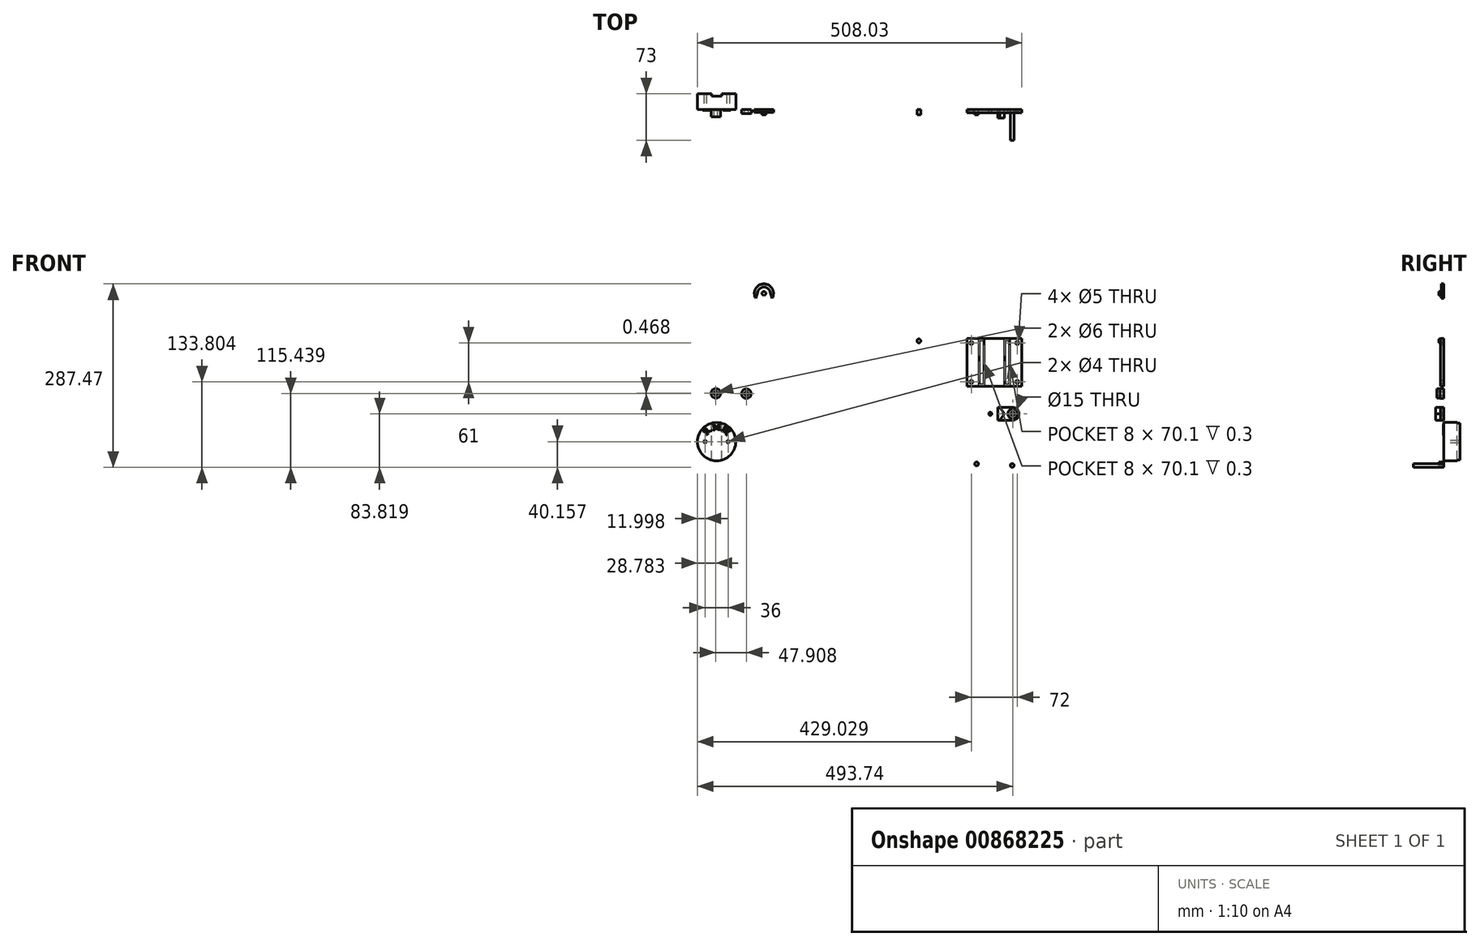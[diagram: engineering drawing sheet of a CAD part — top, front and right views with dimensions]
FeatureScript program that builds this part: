
annotation { "Feature Type Name" : "Feature", "Feature Type Description" : "" }
export const myFeature = defineFeature(function(context is Context, id is Id, definition is map)
    precondition{}
    {
        {
            var Q0;
            Q0=qCreatedBy(makeId("Front.planeOp"),FACE);
            var sketch = newSketch(context, id + "F0", { "sketchPlane" : qUnion([Q0])});
            skCircle(sketch, "E0", {"center": v(126.75, 123.56) * mm, "radius": 3 * mm});
            skLineSegment(sketch, "E1", {"start": v(91.75, 73.56) * mm, "end": v(161.75, 73.56) * mm});
            skLineSegment(sketch, "E2", {"start": v(161.75, 73.56) * mm, "end": v(161.75, 74.2) * mm});
            skLineSegment(sketch, "E3", {"start": v(91.75, 73.56) * mm, "end": v(91.75, 74.2) * mm});
            skLineSegment(sketch, "E4", {"start": v(105.95, 87.96) * mm, "end": v(117.15, 126.36) * mm});
            skLineSegment(sketch, "E5", {"start": v(136.35, 126.36) * mm, "end": v(147.55, 87.96) * mm});
            skArc(sketch, "E6", {"start": v(147.55, 87.96) * mm, "mid": v(152.83, 79.2) * mm, "end": v(161.75, 74.2) * mm});
            skArc(sketch, "E7", {"start": v(91.75, 74.2) * mm, "mid": v(100.67, 79.2) * mm, "end": v(105.95, 87.96) * mm});
            skArc(sketch, "E8", {"start": v(136.35, 126.36) * mm, "mid": v(126.75, 133.56) * mm, "end": v(117.15, 126.36) * mm});
            skSolve(sketch);
        }
        {
            var Q0;
            Q0=makeQuery(id+"F0.imprint","IMPRINT",FACE,{"disambiguationData":[TD([[makeQuery(id+"F0.imprint","IMPRINT",EDGE,{"derivedFrom":sQuery(id+"F0.wireOp",EDGE,"E0")}),1.0]])]});
            extrude(context, id + "F1", {"entities" : qUnion([Q0]), "depth" : 8 * mm, "offsetDistance" : 25 * mm});
        }
        {
            var Q0;
            Q0=qCreatedBy(makeId("Front.planeOp"),FACE);
            var sketch = newSketch(context, id + "F2", { "sketchPlane" : qUnion([Q0])});
            skCircle(sketch, "E9", {"center": v(217.17, -69.3) * mm, "radius": 3 * mm});
            skLineSegment(sketch, "E10", {"start": v(222.17, -46.8) * mm, "end": v(228.17, -69.3) * mm});
            skLineSegment(sketch, "E11", {"start": v(228.17, -69.3) * mm, "end": v(222.17, -91.8) * mm});
            skLineSegment(sketch, "E12", {"start": v(89.17, -61.3) * mm, "end": v(196.17, -61.3) * mm});
            skArc(sketch, "E13", {"start": v(89.17, -61.3) * mm, "mid": v(83.52, -63.64) * mm, "end": v(81.17, -69.3) * mm});
            skLineSegment(sketch, "E14", {"start": v(89.17, -77.3) * mm, "end": v(196.17, -77.3) * mm});
            skArc(sketch, "E15", {"start": v(81.17, -69.3) * mm, "mid": v(83.52, -74.96) * mm, "end": v(89.17, -77.3) * mm});
            skLineSegment(sketch, "E16", {"start": v(214.17, -46.8) * mm, "end": v(222.17, -46.8) * mm});
            skLineSegment(sketch, "E17", {"start": v(214.17, -91.8) * mm, "end": v(222.17, -91.8) * mm});
            skLineSegment(sketch, "E18", {"start": v(222.17, -91.8) * mm, "end": v(214.17, -91.8) * mm});
            skLineSegment(sketch, "E19", {"start": v(196.17, -61.3) * mm, "end": v(214.17, -46.8) * mm});
            skLineSegment(sketch, "E20", {"start": v(214.17, -91.8) * mm, "end": v(196.17, -77.3) * mm});
            skSolve(sketch);
        }
        {
            var Q0;
            Q0=makeQuery(id+"F2.imprint","IMPRINT",FACE,{"disambiguationData":[TD([[makeQuery(id+"F2.imprint","IMPRINT",EDGE,{"derivedFrom":sQuery(id+"F2.wireOp",EDGE,"E9")}),1.0]])]});
            extrude(context, id + "F3", {"entities" : qUnion([Q0]), "depth" : 8 * mm, "offsetDistance" : 25 * mm});
        }
        {
            var Q0;
            Q0=qCreatedBy(makeId("Front.planeOp"),FACE);
            var sketch = newSketch(context, id + "F4", { "sketchPlane" : qUnion([Q0])});
            skCircle(sketch, "E21", {"center": v(272.88, -71.54) * mm, "radius": 3 * mm});
            skSolve(sketch);
        }
        {
            var Q0;
            Q0=makeQuery(id+"F4.imprint","IMPRINT",FACE,{"disambiguationData":[TD([[makeQuery(id+"F4.imprint","IMPRINT",EDGE,{"derivedFrom":sQuery(id+"F4.wireOp",EDGE,"E21")}),1.0]])]});
            extrude(context, id + "F5", {"entities" : qUnion([Q0]), "depth" : 48 * mm, "offsetDistance" : 25 * mm});
        }
        {
            var Q0;
            Q0=qCreatedBy(makeId("Front.planeOp"),FACE);
            var sketch = newSketch(context, id + "F6", { "sketchPlane" : qUnion([Q0])});
            skLineSegment(sketch, "E22", {"start": v(-199.9, -17.86) * mm, "end": v(-201.48, -19.46) * mm});
            skLineSegment(sketch, "E23", {"start": v(-201.48, -19.46) * mm, "end": v(-206.3, -18.72) * mm});
            skLineSegment(sketch, "E24", {"start": v(-206.3, -18.72) * mm, "end": v(-206.66, -19.1) * mm});
            skLineSegment(sketch, "E25", {"start": v(-206.66, -19.1) * mm, "end": v(-206.78, -19.21) * mm});
            skLineSegment(sketch, "E26", {"start": v(-206.78, -19.21) * mm, "end": v(-206.92, -19.34) * mm});
            skLineSegment(sketch, "E27", {"start": v(-206.92, -19.34) * mm, "end": v(-205.18, -21.07) * mm});
            skLineSegment(sketch, "E28", {"start": v(-205.18, -21.07) * mm, "end": v(-204.91, -21.32) * mm});
            skLineSegment(sketch, "E29", {"start": v(-204.91, -21.32) * mm, "end": v(-204.8, -21.42) * mm});
            skLineSegment(sketch, "E30", {"start": v(-204.8, -21.42) * mm, "end": v(-204.69, -21.5) * mm});
            skLineSegment(sketch, "E31", {"start": v(-204.69, -21.5) * mm, "end": v(-204.59, -21.56) * mm});
            skLineSegment(sketch, "E32", {"start": v(-204.59, -21.56) * mm, "end": v(-204.5, -21.6) * mm});
            skLineSegment(sketch, "E33", {"start": v(-204.5, -21.6) * mm, "end": v(-204.42, -21.63) * mm});
            skLineSegment(sketch, "E34", {"start": v(-204.42, -21.63) * mm, "end": v(-204.35, -21.64) * mm});
            skLineSegment(sketch, "E35", {"start": v(-204.35, -21.64) * mm, "end": v(-204.26, -21.65) * mm});
            skLineSegment(sketch, "E36", {"start": v(-204.26, -21.65) * mm, "end": v(-204.17, -21.63) * mm});
            skLineSegment(sketch, "E37", {"start": v(-204.17, -21.63) * mm, "end": v(-204.08, -21.61) * mm});
            skLineSegment(sketch, "E38", {"start": v(-204.08, -21.61) * mm, "end": v(-204, -21.58) * mm});
            skLineSegment(sketch, "E39", {"start": v(-204, -21.58) * mm, "end": v(-203.9, -21.53) * mm});
            skLineSegment(sketch, "E40", {"start": v(-203.9, -21.53) * mm, "end": v(-203.82, -21.48) * mm});
            skLineSegment(sketch, "E41", {"start": v(-203.82, -21.48) * mm, "end": v(-203.74, -21.41) * mm});
            skLineSegment(sketch, "E42", {"start": v(-203.74, -21.41) * mm, "end": v(-203.66, -21.33) * mm});
            skLineSegment(sketch, "E43", {"start": v(-203.66, -21.33) * mm, "end": v(-203.42, -21.1) * mm});
            skLineSegment(sketch, "E44", {"start": v(-203.42, -21.1) * mm, "end": v(-203.26, -21.26) * mm});
            skLineSegment(sketch, "E45", {"start": v(-203.26, -21.26) * mm, "end": v(-205.8, -23.83) * mm});
            skLineSegment(sketch, "E46", {"start": v(-205.8, -23.83) * mm, "end": v(-205.97, -23.67) * mm});
            skLineSegment(sketch, "E47", {"start": v(-205.97, -23.67) * mm, "end": v(-205.75, -23.45) * mm});
            skLineSegment(sketch, "E48", {"start": v(-205.75, -23.45) * mm, "end": v(-205.66, -23.35) * mm});
            skLineSegment(sketch, "E49", {"start": v(-205.66, -23.35) * mm, "end": v(-205.59, -23.25) * mm});
            skLineSegment(sketch, "E50", {"start": v(-205.59, -23.25) * mm, "end": v(-205.53, -23.16) * mm});
            skLineSegment(sketch, "E51", {"start": v(-205.53, -23.16) * mm, "end": v(-205.49, -23.06) * mm});
            skLineSegment(sketch, "E52", {"start": v(-205.49, -23.06) * mm, "end": v(-205.46, -22.96) * mm});
            skLineSegment(sketch, "E53", {"start": v(-205.46, -22.96) * mm, "end": v(-205.44, -22.86) * mm});
            skLineSegment(sketch, "E54", {"start": v(-205.44, -22.86) * mm, "end": v(-205.44, -22.76) * mm});
            skLineSegment(sketch, "E55", {"start": v(-205.44, -22.76) * mm, "end": v(-205.46, -22.66) * mm});
            skLineSegment(sketch, "E56", {"start": v(-205.46, -22.66) * mm, "end": v(-205.47, -22.6) * mm});
            skLineSegment(sketch, "E57", {"start": v(-205.47, -22.6) * mm, "end": v(-205.5, -22.52) * mm});
            skLineSegment(sketch, "E58", {"start": v(-205.5, -22.52) * mm, "end": v(-205.62, -22.36) * mm});
            skLineSegment(sketch, "E59", {"start": v(-205.62, -22.36) * mm, "end": v(-205.79, -22.15) * mm});
            skLineSegment(sketch, "E60", {"start": v(-205.79, -22.15) * mm, "end": v(-206.01, -21.92) * mm});
            skLineSegment(sketch, "E61", {"start": v(-206.01, -21.92) * mm, "end": v(-209.9, -18.08) * mm});
            skLineSegment(sketch, "E62", {"start": v(-209.9, -18.08) * mm, "end": v(-210.16, -17.83) * mm});
            skLineSegment(sketch, "E63", {"start": v(-210.16, -17.83) * mm, "end": v(-210.28, -17.74) * mm});
            skLineSegment(sketch, "E64", {"start": v(-210.28, -17.74) * mm, "end": v(-210.39, -17.65) * mm});
            skLineSegment(sketch, "E65", {"start": v(-210.39, -17.65) * mm, "end": v(-210.49, -17.6) * mm});
            skLineSegment(sketch, "E66", {"start": v(-210.49, -17.6) * mm, "end": v(-210.57, -17.55) * mm});
            skLineSegment(sketch, "E67", {"start": v(-210.57, -17.55) * mm, "end": v(-210.65, -17.52) * mm});
            skLineSegment(sketch, "E68", {"start": v(-210.65, -17.52) * mm, "end": v(-210.72, -17.5) * mm});
            skLineSegment(sketch, "E69", {"start": v(-210.72, -17.5) * mm, "end": v(-210.81, -17.5) * mm});
            skLineSegment(sketch, "E70", {"start": v(-210.81, -17.5) * mm, "end": v(-210.9, -17.52) * mm});
            skLineSegment(sketch, "E71", {"start": v(-210.9, -17.52) * mm, "end": v(-211, -17.54) * mm});
            skLineSegment(sketch, "E72", {"start": v(-211, -17.54) * mm, "end": v(-211.08, -17.58) * mm});
            skLineSegment(sketch, "E73", {"start": v(-211.08, -17.58) * mm, "end": v(-211.17, -17.62) * mm});
            skLineSegment(sketch, "E74", {"start": v(-211.17, -17.62) * mm, "end": v(-211.26, -17.68) * mm});
            skLineSegment(sketch, "E75", {"start": v(-211.26, -17.68) * mm, "end": v(-211.34, -17.75) * mm});
            skLineSegment(sketch, "E76", {"start": v(-211.34, -17.75) * mm, "end": v(-211.43, -17.83) * mm});
            skLineSegment(sketch, "E77", {"start": v(-211.43, -17.83) * mm, "end": v(-211.65, -18.05) * mm});
            skLineSegment(sketch, "E78", {"start": v(-211.65, -18.05) * mm, "end": v(-211.81, -17.9) * mm});
            skLineSegment(sketch, "E79", {"start": v(-211.81, -17.9) * mm, "end": v(-209.65, -15.7) * mm});
            skLineSegment(sketch, "E80", {"start": v(-209.65, -15.7) * mm, "end": v(-209.2, -15.26) * mm});
            skLineSegment(sketch, "E81", {"start": v(-209.2, -15.26) * mm, "end": v(-208.99, -15.07) * mm});
            skLineSegment(sketch, "E82", {"start": v(-208.99, -15.07) * mm, "end": v(-208.8, -14.9) * mm});
            skLineSegment(sketch, "E83", {"start": v(-208.8, -14.9) * mm, "end": v(-208.6, -14.76) * mm});
            skLineSegment(sketch, "E84", {"start": v(-208.6, -14.76) * mm, "end": v(-208.43, -14.63) * mm});
            skLineSegment(sketch, "E85", {"start": v(-208.43, -14.63) * mm, "end": v(-208.27, -14.52) * mm});
            skLineSegment(sketch, "E86", {"start": v(-208.27, -14.52) * mm, "end": v(-208.11, -14.43) * mm});
            skLineSegment(sketch, "E87", {"start": v(-208.11, -14.43) * mm, "end": v(-207.96, -14.36) * mm});
            skLineSegment(sketch, "E88", {"start": v(-207.96, -14.36) * mm, "end": v(-207.81, -14.3) * mm});
            skLineSegment(sketch, "E89", {"start": v(-207.81, -14.3) * mm, "end": v(-207.66, -14.24) * mm});
            skLineSegment(sketch, "E90", {"start": v(-207.66, -14.24) * mm, "end": v(-207.5, -14.2) * mm});
            skLineSegment(sketch, "E91", {"start": v(-207.5, -14.2) * mm, "end": v(-207.34, -14.18) * mm});
            skLineSegment(sketch, "E92", {"start": v(-207.34, -14.18) * mm, "end": v(-207.17, -14.16) * mm});
            skLineSegment(sketch, "E93", {"start": v(-207.17, -14.16) * mm, "end": v(-207, -14.16) * mm});
            skLineSegment(sketch, "E94", {"start": v(-207, -14.16) * mm, "end": v(-206.84, -14.17) * mm});
            skLineSegment(sketch, "E95", {"start": v(-206.84, -14.17) * mm, "end": v(-206.67, -14.19) * mm});
            skLineSegment(sketch, "E96", {"start": v(-206.67, -14.19) * mm, "end": v(-206.5, -14.22) * mm});
            skLineSegment(sketch, "E97", {"start": v(-206.5, -14.22) * mm, "end": v(-206.34, -14.27) * mm});
            skLineSegment(sketch, "E98", {"start": v(-206.34, -14.27) * mm, "end": v(-206.2, -14.33) * mm});
            skLineSegment(sketch, "E99", {"start": v(-206.2, -14.33) * mm, "end": v(-206.04, -14.41) * mm});
            skLineSegment(sketch, "E100", {"start": v(-206.04, -14.41) * mm, "end": v(-205.9, -14.5) * mm});
            skLineSegment(sketch, "E101", {"start": v(-205.9, -14.5) * mm, "end": v(-205.76, -14.61) * mm});
            skLineSegment(sketch, "E102", {"start": v(-205.76, -14.61) * mm, "end": v(-205.63, -14.73) * mm});
            skLineSegment(sketch, "E103", {"start": v(-205.63, -14.73) * mm, "end": v(-205.5, -14.87) * mm});
            skLineSegment(sketch, "E104", {"start": v(-205.5, -14.87) * mm, "end": v(-205.39, -15.02) * mm});
            skLineSegment(sketch, "E105", {"start": v(-205.39, -15.02) * mm, "end": v(-205.29, -15.17) * mm});
            skLineSegment(sketch, "E106", {"start": v(-205.29, -15.17) * mm, "end": v(-205.2, -15.33) * mm});
            skLineSegment(sketch, "E107", {"start": v(-205.2, -15.33) * mm, "end": v(-205.14, -15.5) * mm});
            skLineSegment(sketch, "E108", {"start": v(-205.14, -15.5) * mm, "end": v(-205.08, -15.68) * mm});
            skLineSegment(sketch, "E109", {"start": v(-205.08, -15.68) * mm, "end": v(-205.05, -15.86) * mm});
            skLineSegment(sketch, "E110", {"start": v(-205.05, -15.86) * mm, "end": v(-205.03, -16.04) * mm});
            skLineSegment(sketch, "E111", {"start": v(-205.03, -16.04) * mm, "end": v(-205.02, -16.24) * mm});
            skLineSegment(sketch, "E112", {"start": v(-205.02, -16.24) * mm, "end": v(-205.04, -16.44) * mm});
            skLineSegment(sketch, "E113", {"start": v(-205.04, -16.44) * mm, "end": v(-205.08, -16.64) * mm});
            skLineSegment(sketch, "E114", {"start": v(-205.08, -16.64) * mm, "end": v(-205.13, -16.85) * mm});
            skLineSegment(sketch, "E115", {"start": v(-205.13, -16.85) * mm, "end": v(-205.21, -17.06) * mm});
            skLineSegment(sketch, "E116", {"start": v(-205.21, -17.06) * mm, "end": v(-205.3, -17.28) * mm});
            skLineSegment(sketch, "E117", {"start": v(-205.3, -17.28) * mm, "end": v(-205.42, -17.5) * mm});
            skLineSegment(sketch, "E118", {"start": v(-205.42, -17.5) * mm, "end": v(-205.56, -17.73) * mm});
            skLineSegment(sketch, "E119", {"start": v(-205.56, -17.73) * mm, "end": v(-202.6, -18.2) * mm});
            skLineSegment(sketch, "E120", {"start": v(-202.6, -18.2) * mm, "end": v(-202.13, -18.26) * mm});
            skLineSegment(sketch, "E121", {"start": v(-202.13, -18.26) * mm, "end": v(-201.72, -18.3) * mm});
            skLineSegment(sketch, "E122", {"start": v(-201.72, -18.3) * mm, "end": v(-201.54, -18.3) * mm});
            skLineSegment(sketch, "E123", {"start": v(-201.54, -18.3) * mm, "end": v(-201.38, -18.29) * mm});
            skLineSegment(sketch, "E124", {"start": v(-201.38, -18.29) * mm, "end": v(-201.23, -18.27) * mm});
            skLineSegment(sketch, "E125", {"start": v(-201.23, -18.27) * mm, "end": v(-201.1, -18.25) * mm});
            skLineSegment(sketch, "E126", {"start": v(-201.1, -18.25) * mm, "end": v(-200.97, -18.21) * mm});
            skLineSegment(sketch, "E127", {"start": v(-200.97, -18.21) * mm, "end": v(-200.84, -18.17) * mm});
            skLineSegment(sketch, "E128", {"start": v(-200.84, -18.17) * mm, "end": v(-200.72, -18.12) * mm});
            skLineSegment(sketch, "E129", {"start": v(-200.72, -18.12) * mm, "end": v(-200.59, -18.05) * mm});
            skLineSegment(sketch, "E130", {"start": v(-200.59, -18.05) * mm, "end": v(-200.46, -17.98) * mm});
            skLineSegment(sketch, "E131", {"start": v(-200.46, -17.98) * mm, "end": v(-200.32, -17.9) * mm});
            skLineSegment(sketch, "E132", {"start": v(-200.32, -17.9) * mm, "end": v(-200.06, -17.7) * mm});
            skLineSegment(sketch, "E133", {"start": v(-200.06, -17.7) * mm, "end": v(-199.9, -17.86) * mm});
            skLineSegment(sketch, "E134", {"start": v(-207.2, -19.07) * mm, "end": v(-207.06, -18.92) * mm});
            skLineSegment(sketch, "E135", {"start": v(-207.06, -18.92) * mm, "end": v(-206.95, -18.83) * mm});
            skLineSegment(sketch, "E136", {"start": v(-206.95, -18.83) * mm, "end": v(-206.75, -18.61) * mm});
            skLineSegment(sketch, "E137", {"start": v(-206.75, -18.61) * mm, "end": v(-206.58, -18.4) * mm});
            skLineSegment(sketch, "E138", {"start": v(-206.58, -18.4) * mm, "end": v(-206.43, -18.19) * mm});
            skLineSegment(sketch, "E139", {"start": v(-206.43, -18.19) * mm, "end": v(-206.3, -17.98) * mm});
            skLineSegment(sketch, "E140", {"start": v(-206.3, -17.98) * mm, "end": v(-206.2, -17.77) * mm});
            skLineSegment(sketch, "E141", {"start": v(-206.2, -17.77) * mm, "end": v(-206.12, -17.57) * mm});
            skLineSegment(sketch, "E142", {"start": v(-206.12, -17.57) * mm, "end": v(-206.07, -17.36) * mm});
            skLineSegment(sketch, "E143", {"start": v(-206.07, -17.36) * mm, "end": v(-206.04, -17.16) * mm});
            skLineSegment(sketch, "E144", {"start": v(-206.04, -17.16) * mm, "end": v(-206.04, -16.96) * mm});
            skLineSegment(sketch, "E145", {"start": v(-206.04, -16.96) * mm, "end": v(-206.05, -16.77) * mm});
            skLineSegment(sketch, "E146", {"start": v(-206.05, -16.77) * mm, "end": v(-206.09, -16.6) * mm});
            skLineSegment(sketch, "E147", {"start": v(-206.09, -16.6) * mm, "end": v(-206.14, -16.42) * mm});
            skLineSegment(sketch, "E148", {"start": v(-206.14, -16.42) * mm, "end": v(-206.22, -16.25) * mm});
            skLineSegment(sketch, "E149", {"start": v(-206.22, -16.25) * mm, "end": v(-206.31, -16.09) * mm});
            skLineSegment(sketch, "E150", {"start": v(-206.31, -16.09) * mm, "end": v(-206.43, -15.93) * mm});
            skLineSegment(sketch, "E151", {"start": v(-206.43, -15.93) * mm, "end": v(-206.56, -15.79) * mm});
            skLineSegment(sketch, "E152", {"start": v(-206.56, -15.79) * mm, "end": v(-206.7, -15.66) * mm});
            skLineSegment(sketch, "E153", {"start": v(-206.7, -15.66) * mm, "end": v(-206.85, -15.54) * mm});
            skLineSegment(sketch, "E154", {"start": v(-206.85, -15.54) * mm, "end": v(-207, -15.45) * mm});
            skLineSegment(sketch, "E155", {"start": v(-207, -15.45) * mm, "end": v(-207.16, -15.37) * mm});
            skLineSegment(sketch, "E156", {"start": v(-207.16, -15.37) * mm, "end": v(-207.32, -15.3) * mm});
            skLineSegment(sketch, "E157", {"start": v(-207.32, -15.3) * mm, "end": v(-207.48, -15.27) * mm});
            skLineSegment(sketch, "E158", {"start": v(-207.48, -15.27) * mm, "end": v(-207.65, -15.24) * mm});
            skLineSegment(sketch, "E159", {"start": v(-207.65, -15.24) * mm, "end": v(-207.82, -15.23) * mm});
            skLineSegment(sketch, "E160", {"start": v(-207.82, -15.23) * mm, "end": v(-208, -15.24) * mm});
            skLineSegment(sketch, "E161", {"start": v(-208, -15.24) * mm, "end": v(-208.17, -15.27) * mm});
            skLineSegment(sketch, "E162", {"start": v(-208.17, -15.27) * mm, "end": v(-208.33, -15.32) * mm});
            skLineSegment(sketch, "E163", {"start": v(-208.33, -15.32) * mm, "end": v(-208.5, -15.38) * mm});
            skLineSegment(sketch, "E164", {"start": v(-208.5, -15.38) * mm, "end": v(-208.65, -15.46) * mm});
            skLineSegment(sketch, "E165", {"start": v(-208.65, -15.46) * mm, "end": v(-208.8, -15.56) * mm});
            skLineSegment(sketch, "E166", {"start": v(-208.8, -15.56) * mm, "end": v(-208.95, -15.68) * mm});
            skLineSegment(sketch, "E167", {"start": v(-208.95, -15.68) * mm, "end": v(-209.1, -15.82) * mm});
            skLineSegment(sketch, "E168", {"start": v(-209.1, -15.82) * mm, "end": v(-209.23, -15.96) * mm});
            skLineSegment(sketch, "E169", {"start": v(-209.23, -15.96) * mm, "end": v(-209.38, -16.14) * mm});
            skLineSegment(sketch, "E170", {"start": v(-209.38, -16.14) * mm, "end": v(-209.53, -16.35) * mm});
            skLineSegment(sketch, "E171", {"start": v(-209.53, -16.35) * mm, "end": v(-209.7, -16.6) * mm});
            skLineSegment(sketch, "E172", {"start": v(-209.7, -16.6) * mm, "end": v(-207.2, -19.07) * mm});
            skLineSegment(sketch, "E173", {"start": v(-198.08, -16.28) * mm, "end": v(-197.95, -16.23) * mm});
            skLineSegment(sketch, "E174", {"start": v(-197.95, -16.23) * mm, "end": v(-197.81, -16.21) * mm});
            skLineSegment(sketch, "E175", {"start": v(-197.81, -16.21) * mm, "end": v(-197.68, -16.22) * mm});
            skLineSegment(sketch, "E176", {"start": v(-197.68, -16.22) * mm, "end": v(-197.55, -16.26) * mm});
            skLineSegment(sketch, "E177", {"start": v(-197.55, -16.26) * mm, "end": v(-197.42, -16.32) * mm});
            skLineSegment(sketch, "E178", {"start": v(-197.42, -16.32) * mm, "end": v(-197.32, -16.4) * mm});
            skLineSegment(sketch, "E179", {"start": v(-197.32, -16.4) * mm, "end": v(-197.23, -16.5) * mm});
            skLineSegment(sketch, "E180", {"start": v(-197.23, -16.5) * mm, "end": v(-197.16, -16.61) * mm});
            skLineSegment(sketch, "E181", {"start": v(-197.16, -16.61) * mm, "end": v(-197.1, -16.74) * mm});
            skLineSegment(sketch, "E182", {"start": v(-197.1, -16.74) * mm, "end": v(-197.09, -16.88) * mm});
            skLineSegment(sketch, "E183", {"start": v(-197.09, -16.88) * mm, "end": v(-197.1, -17) * mm});
            skLineSegment(sketch, "E184", {"start": v(-197.1, -17) * mm, "end": v(-197.13, -17.14) * mm});
            skLineSegment(sketch, "E185", {"start": v(-197.13, -17.14) * mm, "end": v(-197.2, -17.27) * mm});
            skLineSegment(sketch, "E186", {"start": v(-197.2, -17.27) * mm, "end": v(-197.27, -17.38) * mm});
            skLineSegment(sketch, "E187", {"start": v(-197.27, -17.38) * mm, "end": v(-197.37, -17.46) * mm});
            skLineSegment(sketch, "E188", {"start": v(-197.37, -17.46) * mm, "end": v(-197.49, -17.53) * mm});
            skLineSegment(sketch, "E189", {"start": v(-197.49, -17.53) * mm, "end": v(-197.62, -17.58) * mm});
            skLineSegment(sketch, "E190", {"start": v(-197.62, -17.58) * mm, "end": v(-197.75, -17.6) * mm});
            skLineSegment(sketch, "E191", {"start": v(-197.75, -17.6) * mm, "end": v(-197.88, -17.6) * mm});
            skLineSegment(sketch, "E192", {"start": v(-197.88, -17.6) * mm, "end": v(-198.02, -17.56) * mm});
            skLineSegment(sketch, "E193", {"start": v(-198.02, -17.56) * mm, "end": v(-198.14, -17.5) * mm});
            skLineSegment(sketch, "E194", {"start": v(-198.14, -17.5) * mm, "end": v(-198.25, -17.42) * mm});
            skLineSegment(sketch, "E195", {"start": v(-198.25, -17.42) * mm, "end": v(-198.34, -17.32) * mm});
            skLineSegment(sketch, "E196", {"start": v(-198.34, -17.32) * mm, "end": v(-198.4, -17.2) * mm});
            skLineSegment(sketch, "E197", {"start": v(-198.4, -17.2) * mm, "end": v(-198.46, -17.07) * mm});
            skLineSegment(sketch, "E198", {"start": v(-198.46, -17.07) * mm, "end": v(-198.48, -16.94) * mm});
            skLineSegment(sketch, "E199", {"start": v(-198.48, -16.94) * mm, "end": v(-198.47, -16.8) * mm});
            skLineSegment(sketch, "E200", {"start": v(-198.47, -16.8) * mm, "end": v(-198.44, -16.67) * mm});
            skLineSegment(sketch, "E201", {"start": v(-198.44, -16.67) * mm, "end": v(-198.38, -16.55) * mm});
            skLineSegment(sketch, "E202", {"start": v(-198.38, -16.55) * mm, "end": v(-198.3, -16.44) * mm});
            skLineSegment(sketch, "E203", {"start": v(-198.3, -16.44) * mm, "end": v(-198.2, -16.35) * mm});
            skLineSegment(sketch, "E204", {"start": v(-198.2, -16.35) * mm, "end": v(-198.08, -16.28) * mm});
            skLineSegment(sketch, "E205", {"start": v(-190.55, -15.85) * mm, "end": v(-193.93, -8.79) * mm});
            skLineSegment(sketch, "E206", {"start": v(-193.93, -8.79) * mm, "end": v(-193.84, -14.43) * mm});
            skLineSegment(sketch, "E207", {"start": v(-193.84, -14.43) * mm, "end": v(-193.83, -14.79) * mm});
            skLineSegment(sketch, "E208", {"start": v(-193.83, -14.79) * mm, "end": v(-193.8, -15.07) * mm});
            skLineSegment(sketch, "E209", {"start": v(-193.8, -15.07) * mm, "end": v(-193.76, -15.18) * mm});
            skLineSegment(sketch, "E210", {"start": v(-193.76, -15.18) * mm, "end": v(-193.73, -15.27) * mm});
            skLineSegment(sketch, "E211", {"start": v(-193.73, -15.27) * mm, "end": v(-193.7, -15.35) * mm});
            skLineSegment(sketch, "E212", {"start": v(-193.7, -15.35) * mm, "end": v(-193.66, -15.4) * mm});
            skLineSegment(sketch, "E213", {"start": v(-193.66, -15.4) * mm, "end": v(-193.6, -15.46) * mm});
            skLineSegment(sketch, "E214", {"start": v(-193.6, -15.46) * mm, "end": v(-193.52, -15.52) * mm});
            skLineSegment(sketch, "E215", {"start": v(-193.52, -15.52) * mm, "end": v(-193.45, -15.56) * mm});
            skLineSegment(sketch, "E216", {"start": v(-193.45, -15.56) * mm, "end": v(-193.36, -15.6) * mm});
            skLineSegment(sketch, "E217", {"start": v(-193.36, -15.6) * mm, "end": v(-193.26, -15.62) * mm});
            skLineSegment(sketch, "E218", {"start": v(-193.26, -15.62) * mm, "end": v(-193.16, -15.64) * mm});
            skLineSegment(sketch, "E219", {"start": v(-193.16, -15.64) * mm, "end": v(-193.05, -15.65) * mm});
            skLineSegment(sketch, "E220", {"start": v(-193.05, -15.65) * mm, "end": v(-192.93, -15.65) * mm});
            skLineSegment(sketch, "E221", {"start": v(-192.93, -15.65) * mm, "end": v(-192.63, -15.65) * mm});
            skLineSegment(sketch, "E222", {"start": v(-192.63, -15.65) * mm, "end": v(-192.62, -15.88) * mm});
            skLineSegment(sketch, "E223", {"start": v(-192.62, -15.88) * mm, "end": v(-195.56, -15.93) * mm});
            skLineSegment(sketch, "E224", {"start": v(-195.56, -15.93) * mm, "end": v(-195.57, -15.7) * mm});
            skLineSegment(sketch, "E225", {"start": v(-195.57, -15.7) * mm, "end": v(-195.27, -15.7) * mm});
            skLineSegment(sketch, "E226", {"start": v(-195.27, -15.7) * mm, "end": v(-195.14, -15.68) * mm});
            skLineSegment(sketch, "E227", {"start": v(-195.14, -15.68) * mm, "end": v(-195.02, -15.67) * mm});
            skLineSegment(sketch, "E228", {"start": v(-195.02, -15.67) * mm, "end": v(-194.91, -15.64) * mm});
            skLineSegment(sketch, "E229", {"start": v(-194.91, -15.64) * mm, "end": v(-194.81, -15.6) * mm});
            skLineSegment(sketch, "E230", {"start": v(-194.81, -15.6) * mm, "end": v(-194.72, -15.56) * mm});
            skLineSegment(sketch, "E231", {"start": v(-194.72, -15.56) * mm, "end": v(-194.64, -15.5) * mm});
            skLineSegment(sketch, "E232", {"start": v(-194.64, -15.5) * mm, "end": v(-194.57, -15.43) * mm});
            skLineSegment(sketch, "E233", {"start": v(-194.57, -15.43) * mm, "end": v(-194.51, -15.35) * mm});
            skLineSegment(sketch, "E234", {"start": v(-194.51, -15.35) * mm, "end": v(-194.48, -15.3) * mm});
            skLineSegment(sketch, "E235", {"start": v(-194.48, -15.3) * mm, "end": v(-194.46, -15.22) * mm});
            skLineSegment(sketch, "E236", {"start": v(-194.46, -15.22) * mm, "end": v(-194.43, -15.13) * mm});
            skLineSegment(sketch, "E237", {"start": v(-194.43, -15.13) * mm, "end": v(-194.42, -15.03) * mm});
            skLineSegment(sketch, "E238", {"start": v(-194.42, -15.03) * mm, "end": v(-194.4, -14.77) * mm});
            skLineSegment(sketch, "E239", {"start": v(-194.4, -14.77) * mm, "end": v(-194.4, -14.44) * mm});
            skLineSegment(sketch, "E240", {"start": v(-194.4, -14.44) * mm, "end": v(-194.48, -8.92) * mm});
            skLineSegment(sketch, "E241", {"start": v(-194.48, -8.92) * mm, "end": v(-194.49, -8.66) * mm});
            skLineSegment(sketch, "E242", {"start": v(-194.49, -8.66) * mm, "end": v(-194.51, -8.44) * mm});
            skLineSegment(sketch, "E243", {"start": v(-194.51, -8.44) * mm, "end": v(-194.56, -8.26) * mm});
            skLineSegment(sketch, "E244", {"start": v(-194.56, -8.26) * mm, "end": v(-194.61, -8.11) * mm});
            skLineSegment(sketch, "E245", {"start": v(-194.61, -8.11) * mm, "end": v(-194.67, -8.03) * mm});
            skLineSegment(sketch, "E246", {"start": v(-194.67, -8.03) * mm, "end": v(-194.74, -7.95) * mm});
            skLineSegment(sketch, "E247", {"start": v(-194.74, -7.95) * mm, "end": v(-194.83, -7.88) * mm});
            skLineSegment(sketch, "E248", {"start": v(-194.83, -7.88) * mm, "end": v(-194.94, -7.82) * mm});
            skLineSegment(sketch, "E249", {"start": v(-194.94, -7.82) * mm, "end": v(-195.07, -7.76) * mm});
            skLineSegment(sketch, "E250", {"start": v(-195.07, -7.76) * mm, "end": v(-195.24, -7.73) * mm});
            skLineSegment(sketch, "E251", {"start": v(-195.24, -7.73) * mm, "end": v(-195.45, -7.71) * mm});
            skLineSegment(sketch, "E252", {"start": v(-195.45, -7.71) * mm, "end": v(-195.7, -7.7) * mm});
            skLineSegment(sketch, "E253", {"start": v(-195.7, -7.7) * mm, "end": v(-195.7, -7.48) * mm});
            skLineSegment(sketch, "E254", {"start": v(-195.7, -7.48) * mm, "end": v(-193.3, -7.44) * mm});
            skLineSegment(sketch, "E255", {"start": v(-193.3, -7.44) * mm, "end": v(-190.13, -14) * mm});
            skLineSegment(sketch, "E256", {"start": v(-190.13, -14) * mm, "end": v(-187.22, -7.35) * mm});
            skLineSegment(sketch, "E257", {"start": v(-187.22, -7.35) * mm, "end": v(-184.83, -7.3) * mm});
            skLineSegment(sketch, "E258", {"start": v(-184.83, -7.3) * mm, "end": v(-184.82, -7.54) * mm});
            skLineSegment(sketch, "E259", {"start": v(-184.82, -7.54) * mm, "end": v(-185.12, -7.54) * mm});
            skLineSegment(sketch, "E260", {"start": v(-185.12, -7.54) * mm, "end": v(-185.25, -7.55) * mm});
            skLineSegment(sketch, "E261", {"start": v(-185.25, -7.55) * mm, "end": v(-185.37, -7.57) * mm});
            skLineSegment(sketch, "E262", {"start": v(-185.37, -7.57) * mm, "end": v(-185.48, -7.6) * mm});
            skLineSegment(sketch, "E263", {"start": v(-185.48, -7.6) * mm, "end": v(-185.58, -7.63) * mm});
            skLineSegment(sketch, "E264", {"start": v(-185.58, -7.63) * mm, "end": v(-185.67, -7.68) * mm});
            skLineSegment(sketch, "E265", {"start": v(-185.67, -7.68) * mm, "end": v(-185.75, -7.74) * mm});
            skLineSegment(sketch, "E266", {"start": v(-185.75, -7.74) * mm, "end": v(-185.82, -7.8) * mm});
            skLineSegment(sketch, "E267", {"start": v(-185.82, -7.8) * mm, "end": v(-185.88, -7.88) * mm});
            skLineSegment(sketch, "E268", {"start": v(-185.88, -7.88) * mm, "end": v(-185.9, -7.94) * mm});
            skLineSegment(sketch, "E269", {"start": v(-185.9, -7.94) * mm, "end": v(-185.94, -8.01) * mm});
            skLineSegment(sketch, "E270", {"start": v(-185.94, -8.01) * mm, "end": v(-185.96, -8.1) * mm});
            skLineSegment(sketch, "E271", {"start": v(-185.96, -8.1) * mm, "end": v(-185.98, -8.2) * mm});
            skLineSegment(sketch, "E272", {"start": v(-185.98, -8.2) * mm, "end": v(-186, -8.47) * mm});
            skLineSegment(sketch, "E273", {"start": v(-186, -8.47) * mm, "end": v(-186, -8.8) * mm});
            skLineSegment(sketch, "E274", {"start": v(-186, -8.8) * mm, "end": v(-185.92, -14.31) * mm});
            skLineSegment(sketch, "E275", {"start": v(-185.92, -14.31) * mm, "end": v(-185.9, -14.66) * mm});
            skLineSegment(sketch, "E276", {"start": v(-185.9, -14.66) * mm, "end": v(-185.88, -14.81) * mm});
            skLineSegment(sketch, "E277", {"start": v(-185.88, -14.81) * mm, "end": v(-185.86, -14.94) * mm});
            skLineSegment(sketch, "E278", {"start": v(-185.86, -14.94) * mm, "end": v(-185.84, -15.06) * mm});
            skLineSegment(sketch, "E279", {"start": v(-185.84, -15.06) * mm, "end": v(-185.8, -15.15) * mm});
            skLineSegment(sketch, "E280", {"start": v(-185.8, -15.15) * mm, "end": v(-185.77, -15.22) * mm});
            skLineSegment(sketch, "E281", {"start": v(-185.77, -15.22) * mm, "end": v(-185.73, -15.28) * mm});
            skLineSegment(sketch, "E282", {"start": v(-185.73, -15.28) * mm, "end": v(-185.66, -15.34) * mm});
            skLineSegment(sketch, "E283", {"start": v(-185.66, -15.34) * mm, "end": v(-185.6, -15.4) * mm});
            skLineSegment(sketch, "E284", {"start": v(-185.6, -15.4) * mm, "end": v(-185.51, -15.44) * mm});
            skLineSegment(sketch, "E285", {"start": v(-185.51, -15.44) * mm, "end": v(-185.43, -15.47) * mm});
            skLineSegment(sketch, "E286", {"start": v(-185.43, -15.47) * mm, "end": v(-185.33, -15.5) * mm});
            skLineSegment(sketch, "E287", {"start": v(-185.33, -15.5) * mm, "end": v(-185.23, -15.52) * mm});
            skLineSegment(sketch, "E288", {"start": v(-185.23, -15.52) * mm, "end": v(-185.11, -15.53) * mm});
            skLineSegment(sketch, "E289", {"start": v(-185.11, -15.53) * mm, "end": v(-185, -15.53) * mm});
            skLineSegment(sketch, "E290", {"start": v(-185, -15.53) * mm, "end": v(-184.7, -15.53) * mm});
            skLineSegment(sketch, "E291", {"start": v(-184.7, -15.53) * mm, "end": v(-184.7, -15.76) * mm});
            skLineSegment(sketch, "E292", {"start": v(-184.7, -15.76) * mm, "end": v(-188.29, -15.81) * mm});
            skLineSegment(sketch, "E293", {"start": v(-188.29, -15.81) * mm, "end": v(-188.29, -15.58) * mm});
            skLineSegment(sketch, "E294", {"start": v(-188.29, -15.58) * mm, "end": v(-188, -15.58) * mm});
            skLineSegment(sketch, "E295", {"start": v(-188, -15.58) * mm, "end": v(-187.86, -15.57) * mm});
            skLineSegment(sketch, "E296", {"start": v(-187.86, -15.57) * mm, "end": v(-187.74, -15.55) * mm});
            skLineSegment(sketch, "E297", {"start": v(-187.74, -15.55) * mm, "end": v(-187.63, -15.53) * mm});
            skLineSegment(sketch, "E298", {"start": v(-187.63, -15.53) * mm, "end": v(-187.53, -15.5) * mm});
            skLineSegment(sketch, "E299", {"start": v(-187.53, -15.5) * mm, "end": v(-187.44, -15.44) * mm});
            skLineSegment(sketch, "E300", {"start": v(-187.44, -15.44) * mm, "end": v(-187.36, -15.39) * mm});
            skLineSegment(sketch, "E301", {"start": v(-187.36, -15.39) * mm, "end": v(-187.3, -15.32) * mm});
            skLineSegment(sketch, "E302", {"start": v(-187.3, -15.32) * mm, "end": v(-187.23, -15.24) * mm});
            skLineSegment(sketch, "E303", {"start": v(-187.23, -15.24) * mm, "end": v(-187.2, -15.18) * mm});
            skLineSegment(sketch, "E304", {"start": v(-187.2, -15.18) * mm, "end": v(-187.18, -15.1) * mm});
            skLineSegment(sketch, "E305", {"start": v(-187.18, -15.1) * mm, "end": v(-187.15, -15.02) * mm});
            skLineSegment(sketch, "E306", {"start": v(-187.15, -15.02) * mm, "end": v(-187.14, -14.91) * mm});
            skLineSegment(sketch, "E307", {"start": v(-187.14, -14.91) * mm, "end": v(-187.12, -14.65) * mm});
            skLineSegment(sketch, "E308", {"start": v(-187.12, -14.65) * mm, "end": v(-187.11, -14.33) * mm});
            skLineSegment(sketch, "E309", {"start": v(-187.11, -14.33) * mm, "end": v(-187.2, -8.68) * mm});
            skLineSegment(sketch, "E310", {"start": v(-187.2, -8.68) * mm, "end": v(-190.35, -15.85) * mm});
            skLineSegment(sketch, "E311", {"start": v(-190.35, -15.85) * mm, "end": v(-190.55, -15.85) * mm});
            skLineSegment(sketch, "E312", {"start": v(-182.17, -16.31) * mm, "end": v(-182.05, -16.38) * mm});
            skLineSegment(sketch, "E313", {"start": v(-182.05, -16.38) * mm, "end": v(-181.95, -16.47) * mm});
            skLineSegment(sketch, "E314", {"start": v(-181.95, -16.47) * mm, "end": v(-181.87, -16.58) * mm});
            skLineSegment(sketch, "E315", {"start": v(-181.87, -16.58) * mm, "end": v(-181.82, -16.7) * mm});
            skLineSegment(sketch, "E316", {"start": v(-181.82, -16.7) * mm, "end": v(-181.78, -16.84) * mm});
            skLineSegment(sketch, "E317", {"start": v(-181.78, -16.84) * mm, "end": v(-181.78, -16.97) * mm});
            skLineSegment(sketch, "E318", {"start": v(-181.78, -16.97) * mm, "end": v(-181.8, -17.1) * mm});
            skLineSegment(sketch, "E319", {"start": v(-181.8, -17.1) * mm, "end": v(-181.85, -17.23) * mm});
            skLineSegment(sketch, "E320", {"start": v(-181.85, -17.23) * mm, "end": v(-181.92, -17.35) * mm});
            skLineSegment(sketch, "E321", {"start": v(-181.92, -17.35) * mm, "end": v(-182.01, -17.45) * mm});
            skLineSegment(sketch, "E322", {"start": v(-182.01, -17.45) * mm, "end": v(-182.12, -17.53) * mm});
            skLineSegment(sketch, "E323", {"start": v(-182.12, -17.53) * mm, "end": v(-182.24, -17.59) * mm});
            skLineSegment(sketch, "E324", {"start": v(-182.24, -17.59) * mm, "end": v(-182.38, -17.62) * mm});
            skLineSegment(sketch, "E325", {"start": v(-182.38, -17.62) * mm, "end": v(-182.51, -17.63) * mm});
            skLineSegment(sketch, "E326", {"start": v(-182.51, -17.63) * mm, "end": v(-182.64, -17.6) * mm});
            skLineSegment(sketch, "E327", {"start": v(-182.64, -17.6) * mm, "end": v(-182.77, -17.56) * mm});
            skLineSegment(sketch, "E328", {"start": v(-182.77, -17.56) * mm, "end": v(-182.9, -17.48) * mm});
            skLineSegment(sketch, "E329", {"start": v(-182.9, -17.48) * mm, "end": v(-183, -17.4) * mm});
            skLineSegment(sketch, "E330", {"start": v(-183, -17.4) * mm, "end": v(-183.07, -17.29) * mm});
            skLineSegment(sketch, "E331", {"start": v(-183.07, -17.29) * mm, "end": v(-183.13, -17.16) * mm});
            skLineSegment(sketch, "E332", {"start": v(-183.13, -17.16) * mm, "end": v(-183.16, -17.03) * mm});
            skLineSegment(sketch, "E333", {"start": v(-183.16, -17.03) * mm, "end": v(-183.17, -16.9) * mm});
            skLineSegment(sketch, "E334", {"start": v(-183.17, -16.9) * mm, "end": v(-183.14, -16.76) * mm});
            skLineSegment(sketch, "E335", {"start": v(-183.14, -16.76) * mm, "end": v(-183.1, -16.63) * mm});
            skLineSegment(sketch, "E336", {"start": v(-183.1, -16.63) * mm, "end": v(-183.02, -16.51) * mm});
            skLineSegment(sketch, "E337", {"start": v(-183.02, -16.51) * mm, "end": v(-182.93, -16.41) * mm});
            skLineSegment(sketch, "E338", {"start": v(-182.93, -16.41) * mm, "end": v(-182.82, -16.33) * mm});
            skLineSegment(sketch, "E339", {"start": v(-182.82, -16.33) * mm, "end": v(-182.7, -16.28) * mm});
            skLineSegment(sketch, "E340", {"start": v(-182.7, -16.28) * mm, "end": v(-182.57, -16.25) * mm});
            skLineSegment(sketch, "E341", {"start": v(-182.57, -16.25) * mm, "end": v(-182.43, -16.24) * mm});
            skLineSegment(sketch, "E342", {"start": v(-182.43, -16.24) * mm, "end": v(-182.3, -16.26) * mm});
            skLineSegment(sketch, "E343", {"start": v(-182.3, -16.26) * mm, "end": v(-182.17, -16.31) * mm});
            skLineSegment(sketch, "E344", {"start": v(-168.34, -17.37) * mm, "end": v(-168.48, -17.55) * mm});
            skLineSegment(sketch, "E345", {"start": v(-168.48, -17.55) * mm, "end": v(-168.6, -17.45) * mm});
            skLineSegment(sketch, "E346", {"start": v(-168.6, -17.45) * mm, "end": v(-168.73, -17.38) * mm});
            skLineSegment(sketch, "E347", {"start": v(-168.73, -17.38) * mm, "end": v(-168.85, -17.33) * mm});
            skLineSegment(sketch, "E348", {"start": v(-168.85, -17.33) * mm, "end": v(-168.97, -17.3) * mm});
            skLineSegment(sketch, "E349", {"start": v(-168.97, -17.3) * mm, "end": v(-169.1, -17.3) * mm});
            skLineSegment(sketch, "E350", {"start": v(-169.1, -17.3) * mm, "end": v(-169.24, -17.3) * mm});
            skLineSegment(sketch, "E351", {"start": v(-169.24, -17.3) * mm, "end": v(-169.39, -17.34) * mm});
            skLineSegment(sketch, "E352", {"start": v(-169.39, -17.34) * mm, "end": v(-169.56, -17.4) * mm});
            skLineSegment(sketch, "E353", {"start": v(-169.56, -17.4) * mm, "end": v(-169.7, -17.46) * mm});
            skLineSegment(sketch, "E354", {"start": v(-169.7, -17.46) * mm, "end": v(-169.91, -17.58) * mm});
            skLineSegment(sketch, "E355", {"start": v(-169.91, -17.58) * mm, "end": v(-170.19, -17.74) * mm});
            skLineSegment(sketch, "E356", {"start": v(-170.19, -17.74) * mm, "end": v(-170.52, -17.95) * mm});
            skLineSegment(sketch, "E357", {"start": v(-170.52, -17.95) * mm, "end": v(-176.66, -21.73) * mm});
            skLineSegment(sketch, "E358", {"start": v(-176.66, -21.73) * mm, "end": v(-176.85, -21.57) * mm});
            skLineSegment(sketch, "E359", {"start": v(-176.85, -21.57) * mm, "end": v(-174.92, -16.17) * mm});
            skLineSegment(sketch, "E360", {"start": v(-174.92, -16.17) * mm, "end": v(-179.82, -19.14) * mm});
            skLineSegment(sketch, "E361", {"start": v(-179.82, -19.14) * mm, "end": v(-180, -19) * mm});
            skLineSegment(sketch, "E362", {"start": v(-180, -19) * mm, "end": v(-177.5, -11.97) * mm});
            skLineSegment(sketch, "E363", {"start": v(-177.5, -11.97) * mm, "end": v(-177.27, -11.34) * mm});
            skLineSegment(sketch, "E364", {"start": v(-177.27, -11.34) * mm, "end": v(-177.18, -11.03) * mm});
            skLineSegment(sketch, "E365", {"start": v(-177.18, -11.03) * mm, "end": v(-177.16, -10.9) * mm});
            skLineSegment(sketch, "E366", {"start": v(-177.16, -10.9) * mm, "end": v(-177.16, -10.78) * mm});
            skLineSegment(sketch, "E367", {"start": v(-177.16, -10.78) * mm, "end": v(-177.18, -10.66) * mm});
            skLineSegment(sketch, "E368", {"start": v(-177.18, -10.66) * mm, "end": v(-177.22, -10.54) * mm});
            skLineSegment(sketch, "E369", {"start": v(-177.22, -10.54) * mm, "end": v(-177.28, -10.43) * mm});
            skLineSegment(sketch, "E370", {"start": v(-177.28, -10.43) * mm, "end": v(-177.36, -10.31) * mm});
            skLineSegment(sketch, "E371", {"start": v(-177.36, -10.31) * mm, "end": v(-177.46, -10.2) * mm});
            skLineSegment(sketch, "E372", {"start": v(-177.46, -10.2) * mm, "end": v(-177.6, -10.08) * mm});
            skLineSegment(sketch, "E373", {"start": v(-177.6, -10.08) * mm, "end": v(-177.45, -9.9) * mm});
            skLineSegment(sketch, "E374", {"start": v(-177.45, -9.9) * mm, "end": v(-175.03, -11.89) * mm});
            skLineSegment(sketch, "E375", {"start": v(-175.03, -11.89) * mm, "end": v(-175.17, -12.07) * mm});
            skLineSegment(sketch, "E376", {"start": v(-175.17, -12.07) * mm, "end": v(-175.3, -11.97) * mm});
            skLineSegment(sketch, "E377", {"start": v(-175.3, -11.97) * mm, "end": v(-175.42, -11.88) * mm});
            skLineSegment(sketch, "E378", {"start": v(-175.42, -11.88) * mm, "end": v(-175.54, -11.82) * mm});
            skLineSegment(sketch, "E379", {"start": v(-175.54, -11.82) * mm, "end": v(-175.66, -11.78) * mm});
            skLineSegment(sketch, "E380", {"start": v(-175.66, -11.78) * mm, "end": v(-175.78, -11.77) * mm});
            skLineSegment(sketch, "E381", {"start": v(-175.78, -11.77) * mm, "end": v(-175.88, -11.78) * mm});
            skLineSegment(sketch, "E382", {"start": v(-175.88, -11.78) * mm, "end": v(-175.98, -11.81) * mm});
            skLineSegment(sketch, "E383", {"start": v(-175.98, -11.81) * mm, "end": v(-176.07, -11.86) * mm});
            skLineSegment(sketch, "E384", {"start": v(-176.07, -11.86) * mm, "end": v(-176.14, -11.94) * mm});
            skLineSegment(sketch, "E385", {"start": v(-176.14, -11.94) * mm, "end": v(-176.22, -12.06) * mm});
            skLineSegment(sketch, "E386", {"start": v(-176.22, -12.06) * mm, "end": v(-176.31, -12.26) * mm});
            skLineSegment(sketch, "E387", {"start": v(-176.31, -12.26) * mm, "end": v(-176.43, -12.53) * mm});
            skLineSegment(sketch, "E388", {"start": v(-176.43, -12.53) * mm, "end": v(-176.56, -12.89) * mm});
            skLineSegment(sketch, "E389", {"start": v(-176.56, -12.89) * mm, "end": v(-178.28, -17.6) * mm});
            skLineSegment(sketch, "E390", {"start": v(-178.28, -17.6) * mm, "end": v(-174.64, -15.38) * mm});
            skLineSegment(sketch, "E391", {"start": v(-174.64, -15.38) * mm, "end": v(-174.38, -14.67) * mm});
            skLineSegment(sketch, "E392", {"start": v(-174.38, -14.67) * mm, "end": v(-174.18, -14.1) * mm});
            skLineSegment(sketch, "E393", {"start": v(-174.18, -14.1) * mm, "end": v(-174.14, -13.95) * mm});
            skLineSegment(sketch, "E394", {"start": v(-174.14, -13.95) * mm, "end": v(-174.1, -13.8) * mm});
            skLineSegment(sketch, "E395", {"start": v(-174.1, -13.8) * mm, "end": v(-174.08, -13.64) * mm});
            skLineSegment(sketch, "E396", {"start": v(-174.08, -13.64) * mm, "end": v(-174.06, -13.5) * mm});
            skLineSegment(sketch, "E397", {"start": v(-174.06, -13.5) * mm, "end": v(-174.06, -13.35) * mm});
            skLineSegment(sketch, "E398", {"start": v(-174.06, -13.35) * mm, "end": v(-174.09, -13.22) * mm});
            skLineSegment(sketch, "E399", {"start": v(-174.09, -13.22) * mm, "end": v(-174.15, -13.04) * mm});
            skLineSegment(sketch, "E400", {"start": v(-174.15, -13.04) * mm, "end": v(-174.22, -12.9) * mm});
            skLineSegment(sketch, "E401", {"start": v(-174.22, -12.9) * mm, "end": v(-174.27, -12.84) * mm});
            skLineSegment(sketch, "E402", {"start": v(-174.27, -12.84) * mm, "end": v(-174.32, -12.77) * mm});
            skLineSegment(sketch, "E403", {"start": v(-174.32, -12.77) * mm, "end": v(-174.5, -12.63) * mm});
            skLineSegment(sketch, "E404", {"start": v(-174.5, -12.63) * mm, "end": v(-174.34, -12.45) * mm});
            skLineSegment(sketch, "E405", {"start": v(-174.34, -12.45) * mm, "end": v(-171.8, -14.53) * mm});
            skLineSegment(sketch, "E406", {"start": v(-171.8, -14.53) * mm, "end": v(-171.94, -14.71) * mm});
            skLineSegment(sketch, "E407", {"start": v(-171.94, -14.71) * mm, "end": v(-172.12, -14.57) * mm});
            skLineSegment(sketch, "E408", {"start": v(-172.12, -14.57) * mm, "end": v(-172.25, -14.47) * mm});
            skLineSegment(sketch, "E409", {"start": v(-172.25, -14.47) * mm, "end": v(-172.38, -14.4) * mm});
            skLineSegment(sketch, "E410", {"start": v(-172.38, -14.4) * mm, "end": v(-172.5, -14.37) * mm});
            skLineSegment(sketch, "E411", {"start": v(-172.5, -14.37) * mm, "end": v(-172.6, -14.36) * mm});
            skLineSegment(sketch, "E412", {"start": v(-172.6, -14.36) * mm, "end": v(-172.71, -14.38) * mm});
            skLineSegment(sketch, "E413", {"start": v(-172.71, -14.38) * mm, "end": v(-172.81, -14.42) * mm});
            skLineSegment(sketch, "E414", {"start": v(-172.81, -14.42) * mm, "end": v(-172.9, -14.48) * mm});
            skLineSegment(sketch, "E415", {"start": v(-172.9, -14.48) * mm, "end": v(-173, -14.57) * mm});
            skLineSegment(sketch, "E416", {"start": v(-173, -14.57) * mm, "end": v(-173.1, -14.73) * mm});
            skLineSegment(sketch, "E417", {"start": v(-173.1, -14.73) * mm, "end": v(-173.21, -14.95) * mm});
            skLineSegment(sketch, "E418", {"start": v(-173.21, -14.95) * mm, "end": v(-173.34, -15.25) * mm});
            skLineSegment(sketch, "E419", {"start": v(-173.34, -15.25) * mm, "end": v(-173.48, -15.6) * mm});
            skLineSegment(sketch, "E420", {"start": v(-173.48, -15.6) * mm, "end": v(-175.13, -20.19) * mm});
            skLineSegment(sketch, "E421", {"start": v(-175.13, -20.19) * mm, "end": v(-170.94, -17.6) * mm});
            skLineSegment(sketch, "E422", {"start": v(-170.94, -17.6) * mm, "end": v(-170.62, -17.4) * mm});
            skLineSegment(sketch, "E423", {"start": v(-170.62, -17.4) * mm, "end": v(-170.37, -17.23) * mm});
            skLineSegment(sketch, "E424", {"start": v(-170.37, -17.23) * mm, "end": v(-170.17, -17.08) * mm});
            skLineSegment(sketch, "E425", {"start": v(-170.17, -17.08) * mm, "end": v(-170.05, -16.95) * mm});
            skLineSegment(sketch, "E426", {"start": v(-170.05, -16.95) * mm, "end": v(-170, -16.9) * mm});
            skLineSegment(sketch, "E427", {"start": v(-170, -16.9) * mm, "end": v(-169.98, -16.83) * mm});
            skLineSegment(sketch, "E428", {"start": v(-169.98, -16.83) * mm, "end": v(-169.96, -16.76) * mm});
            skLineSegment(sketch, "E429", {"start": v(-169.96, -16.76) * mm, "end": v(-169.95, -16.69) * mm});
            skLineSegment(sketch, "E430", {"start": v(-169.95, -16.69) * mm, "end": v(-169.95, -16.61) * mm});
            skLineSegment(sketch, "E431", {"start": v(-169.95, -16.61) * mm, "end": v(-169.96, -16.54) * mm});
            skLineSegment(sketch, "E432", {"start": v(-169.96, -16.54) * mm, "end": v(-169.98, -16.47) * mm});
            skLineSegment(sketch, "E433", {"start": v(-169.98, -16.47) * mm, "end": v(-170.01, -16.4) * mm});
            skLineSegment(sketch, "E434", {"start": v(-170.01, -16.4) * mm, "end": v(-170.09, -16.3) * mm});
            skLineSegment(sketch, "E435", {"start": v(-170.09, -16.3) * mm, "end": v(-170.18, -16.18) * mm});
            skLineSegment(sketch, "E436", {"start": v(-170.18, -16.18) * mm, "end": v(-170.3, -16.07) * mm});
            skLineSegment(sketch, "E437", {"start": v(-170.3, -16.07) * mm, "end": v(-170.44, -15.95) * mm});
            skLineSegment(sketch, "E438", {"start": v(-170.44, -15.95) * mm, "end": v(-170.29, -15.77) * mm});
            skLineSegment(sketch, "E439", {"start": v(-170.29, -15.77) * mm, "end": v(-168.34, -17.37) * mm});
            skLineSegment(sketch, "E440", {"start": v(-174, -23.02) * mm, "end": v(-173.92, -23.14) * mm});
            skLineSegment(sketch, "E441", {"start": v(-173.92, -23.14) * mm, "end": v(-173.87, -23.27) * mm});
            skLineSegment(sketch, "E442", {"start": v(-173.87, -23.27) * mm, "end": v(-173.86, -23.4) * mm});
            skLineSegment(sketch, "E443", {"start": v(-173.86, -23.4) * mm, "end": v(-173.86, -23.54) * mm});
            skLineSegment(sketch, "E444", {"start": v(-173.86, -23.54) * mm, "end": v(-173.9, -23.67) * mm});
            skLineSegment(sketch, "E445", {"start": v(-173.9, -23.67) * mm, "end": v(-173.95, -23.8) * mm});
            skLineSegment(sketch, "E446", {"start": v(-173.95, -23.8) * mm, "end": v(-174.03, -23.9) * mm});
            skLineSegment(sketch, "E447", {"start": v(-174.03, -23.9) * mm, "end": v(-174.13, -23.99) * mm});
            skLineSegment(sketch, "E448", {"start": v(-174.13, -23.99) * mm, "end": v(-174.25, -24.06) * mm});
            skLineSegment(sketch, "E449", {"start": v(-174.25, -24.06) * mm, "end": v(-174.38, -24.1) * mm});
            skLineSegment(sketch, "E450", {"start": v(-174.38, -24.1) * mm, "end": v(-174.5, -24.13) * mm});
            skLineSegment(sketch, "E451", {"start": v(-174.5, -24.13) * mm, "end": v(-174.65, -24.12) * mm});
            skLineSegment(sketch, "E452", {"start": v(-174.65, -24.12) * mm, "end": v(-174.78, -24.09) * mm});
            skLineSegment(sketch, "E453", {"start": v(-174.78, -24.09) * mm, "end": v(-174.9, -24.03) * mm});
            skLineSegment(sketch, "E454", {"start": v(-174.9, -24.03) * mm, "end": v(-175, -23.96) * mm});
            skLineSegment(sketch, "E455", {"start": v(-175, -23.96) * mm, "end": v(-175.1, -23.85) * mm});
            skLineSegment(sketch, "E456", {"start": v(-175.1, -23.85) * mm, "end": v(-175.18, -23.73) * mm});
            skLineSegment(sketch, "E457", {"start": v(-175.18, -23.73) * mm, "end": v(-175.22, -23.6) * mm});
            skLineSegment(sketch, "E458", {"start": v(-175.22, -23.6) * mm, "end": v(-175.24, -23.48) * mm});
            skLineSegment(sketch, "E459", {"start": v(-175.24, -23.48) * mm, "end": v(-175.23, -23.34) * mm});
            skLineSegment(sketch, "E460", {"start": v(-175.23, -23.34) * mm, "end": v(-175.2, -23.2) * mm});
            skLineSegment(sketch, "E461", {"start": v(-175.2, -23.2) * mm, "end": v(-175.15, -23.08) * mm});
            skLineSegment(sketch, "E462", {"start": v(-175.15, -23.08) * mm, "end": v(-175.07, -22.98) * mm});
            skLineSegment(sketch, "E463", {"start": v(-175.07, -22.98) * mm, "end": v(-174.96, -22.88) * mm});
            skLineSegment(sketch, "E464", {"start": v(-174.96, -22.88) * mm, "end": v(-174.84, -22.8) * mm});
            skLineSegment(sketch, "E465", {"start": v(-174.84, -22.8) * mm, "end": v(-174.72, -22.76) * mm});
            skLineSegment(sketch, "E466", {"start": v(-174.72, -22.76) * mm, "end": v(-174.59, -22.74) * mm});
            skLineSegment(sketch, "E467", {"start": v(-174.59, -22.74) * mm, "end": v(-174.45, -22.75) * mm});
            skLineSegment(sketch, "E468", {"start": v(-174.45, -22.75) * mm, "end": v(-174.32, -22.78) * mm});
            skLineSegment(sketch, "E469", {"start": v(-174.32, -22.78) * mm, "end": v(-174.2, -22.84) * mm});
            skLineSegment(sketch, "E470", {"start": v(-174.2, -22.84) * mm, "end": v(-174.09, -22.92) * mm});
            skLineSegment(sketch, "E471", {"start": v(-174.09, -22.92) * mm, "end": v(-174, -23.02) * mm});
            skCircle(sketch, "E472", {"center": v(-172.16, -34.38) * mm, "radius": 2 * mm});
            skCircle(sketch, "E473", {"center": v(-208.16, -34.38) * mm, "radius": 2 * mm});
            skCircle(sketch, "E474", {"center": v(-190.16, -34.38) * mm, "radius": 30 * mm});
            skLineSegment(sketch, "E475", {"start": v(-182.16, -63.3) * mm, "end": v(-182.16, -5.47) * mm});
            skLineSegment(sketch, "E476", {"start": v(-198.16, -63.3) * mm, "end": v(-198.16, -5.47) * mm});
            skSolve(sketch);
        }
        {
            var Q0;
            {var subQ4=sQuery(id+"F6.wireOp",EDGE,"E173");Q0=makeQuery(id+"F6.imprint","IMPRINT",FACE,{"disambiguationData":[TD([[makeQuery(id+"F6.imprint","IMPRINT",EDGE,{"derivedFrom":subQ4}),1.0]])]});}
            var Q1;
            Q1=makeQuery(id+"F6.imprint","IMPRINT",FACE,{"disambiguationData":[TD([[makeQuery(id+"F6.imprint","IMPRINT",EDGE,{"derivedFrom":sQuery(id+"F6.wireOp",EDGE,"E205")}),-1.0]])]});
            var Q2;
            {var subQ6=sQuery(id+"F6.wireOp",EDGE,"E324");Q2=makeQuery(id+"F6.imprint","IMPRINT",FACE,{"disambiguationData":[TD([[makeQuery(id+"F6.imprint","IMPRINT",EDGE,{"derivedFrom":subQ6}),-1.0]])]});}
            var Q3;
            {var subQ4=sQuery(id+"F6.wireOp",EDGE,"E173");Q3=makeQuery(id+"F6.imprint","IMPRINT",FACE,{"disambiguationData":[TD([[makeQuery(id+"F6.imprint","IMPRINT",EDGE,{"derivedFrom":subQ4}),-1.0]])]});}
            extrude(context, id + "F7", {"entities" : qUnion([Q0, Q1, Q2, Q3]), "oppositeDirection" : true, "depth" : 21 * mm, "offsetDistance" : 25 * mm});
        }
        {
            var Q0;
            Q0=makeQuery(id+"F6.imprint","IMPRINT",FACE,{"disambiguationData":[TD([[makeQuery(id+"F6.imprint","IMPRINT",EDGE,{"derivedFrom":sQuery(id+"F6.wireOp",EDGE,"E22")}),1.0]])]});
            var Q1;
            {var subQ4=sQuery(id+"F6.wireOp",EDGE,"E313");Q1=makeQuery(id+"F6.imprint","IMPRINT",FACE,{"disambiguationData":[TD([[makeQuery(id+"F6.imprint","IMPRINT",EDGE,{"derivedFrom":subQ4}),1.0]])]});}
            var Q2;
            Q2=makeQuery(id+"F6.imprint","IMPRINT",FACE,{"disambiguationData":[TD([[makeQuery(id+"F6.imprint","IMPRINT",EDGE,{"derivedFrom":sQuery(id+"F6.wireOp",EDGE,"E22")}),-1.0]])]});
            var Q3;
            Q3=makeQuery(id+"F6.imprint","IMPRINT",FACE,{"disambiguationData":[TD([[makeQuery(id+"F6.imprint","IMPRINT",EDGE,{"derivedFrom":sQuery(id+"F6.wireOp",EDGE,"E134")}),1.0]])]});
            var Q4;
            {var subQ1=sQuery(id+"F6.wireOp",EDGE,"E195");Q4=makeQuery(id+"F6.imprint","IMPRINT",FACE,{"disambiguationData":[TD([[makeQuery(id+"F6.imprint","IMPRINT",EDGE,{"derivedFrom":subQ1}),-1.0]])]});}
            var Q5;
            {var subQ5=sQuery(id+"F6.wireOp",EDGE,"E313");Q5=makeQuery(id+"F6.imprint","IMPRINT",FACE,{"disambiguationData":[TD([[makeQuery(id+"F6.imprint","IMPRINT",EDGE,{"derivedFrom":subQ5}),-1.0]])]});}
            var Q6;
            Q6=makeQuery(id+"F6.imprint","IMPRINT",FACE,{"disambiguationData":[TD([[makeQuery(id+"F6.imprint","IMPRINT",EDGE,{"derivedFrom":sQuery(id+"F6.wireOp",EDGE,"E344")}),-1.0]])]});
            var Q7;
            Q7=makeQuery(id+"F6.imprint","IMPRINT",FACE,{"disambiguationData":[TD([[makeQuery(id+"F6.imprint","IMPRINT",EDGE,{"derivedFrom":sQuery(id+"F6.wireOp",EDGE,"E440")}),-1.0]])]});
            extrude(context, id + "F8", {"entities" : qUnion([Q0, Q1, Q2, Q3, Q4, Q5, Q6, Q7]), "oppositeDirection" : true, "depth" : 25 * mm, "offsetDistance" : 25 * mm});
        }
        {
            var Q0;
            Q0=makeQuery(id+"F6.imprint","IMPRINT",FACE,{"disambiguationData":[TD([[makeQuery(id+"F6.imprint","IMPRINT",EDGE,{"derivedFrom":sQuery(id+"F6.wireOp",EDGE,"E22")}),-1.0]])]});
            var Q1;
            {var subQ4=sQuery(id+"F6.wireOp",EDGE,"E173");Q1=makeQuery(id+"F6.imprint","IMPRINT",FACE,{"disambiguationData":[TD([[makeQuery(id+"F6.imprint","IMPRINT",EDGE,{"derivedFrom":subQ4}),-1.0]])]});}
            var Q2;
            {var subQ1=sQuery(id+"F6.wireOp",EDGE,"E195");Q2=makeQuery(id+"F6.imprint","IMPRINT",FACE,{"disambiguationData":[TD([[makeQuery(id+"F6.imprint","IMPRINT",EDGE,{"derivedFrom":subQ1}),-1.0]])]});}
            var Q3;
            Q3=makeQuery(id+"F6.imprint","IMPRINT",FACE,{"disambiguationData":[TD([[makeQuery(id+"F6.imprint","IMPRINT",EDGE,{"derivedFrom":sQuery(id+"F6.wireOp",EDGE,"E205")}),-1.0]])]});
            var Q4;
            {var subQ6=sQuery(id+"F6.wireOp",EDGE,"E324");Q4=makeQuery(id+"F6.imprint","IMPRINT",FACE,{"disambiguationData":[TD([[makeQuery(id+"F6.imprint","IMPRINT",EDGE,{"derivedFrom":subQ6}),-1.0]])]});}
            var Q5;
            {var subQ5=sQuery(id+"F6.wireOp",EDGE,"E313");Q5=makeQuery(id+"F6.imprint","IMPRINT",FACE,{"disambiguationData":[TD([[makeQuery(id+"F6.imprint","IMPRINT",EDGE,{"derivedFrom":subQ5}),-1.0]])]});}
            var Q6;
            Q6=makeQuery(id+"F6.imprint","IMPRINT",FACE,{"disambiguationData":[TD([[makeQuery(id+"F6.imprint","IMPRINT",EDGE,{"derivedFrom":sQuery(id+"F6.wireOp",EDGE,"E344")}),-1.0]])]});
            var Q7;
            Q7=makeQuery(id+"F6.imprint","IMPRINT",FACE,{"disambiguationData":[TD([[makeQuery(id+"F6.imprint","IMPRINT",EDGE,{"derivedFrom":sQuery(id+"F6.wireOp",EDGE,"E440")}),-1.0]])]});
            extrude(context, id + "F9", {"entities" : qUnion([Q0, Q1, Q2, Q3, Q4, Q5, Q6, Q7]), "operationType" : NewBodyOperationType.ADD, "depth" : 1 * mm, "offsetDistance" : 25 * mm});
        }
        {
            var Q0;
            Q0=qCreatedBy(makeId("Front.planeOp"),FACE);
            var sketch = newSketch(context, id + "F10", { "sketchPlane" : qUnion([Q0])});
            skCircle(sketch, "E477", {"center": v(-143.47, 40.9) * mm, "radius": 7.5 * mm});
            skCircle(sketch, "E478", {"center": v(-143.47, 40.9) * mm, "radius": 3 * mm});
            skSolve(sketch);
        }
        {
            var Q0;
            Q0=qCreatedBy(makeId("Front.planeOp"),FACE);
            var sketch = newSketch(context, id + "F11", { "sketchPlane" : qUnion([Q0])});
            skCircle(sketch, "E479", {"center": v(-191.38, 41.37) * mm, "radius": 3 * mm});
            skCircle(sketch, "E480", {"center": v(-191.38, 41.37) * mm, "radius": 7.5 * mm});
            skSolve(sketch);
        }
        {
            var Q0;
            Q0=makeQuery(id+"F10.imprint","IMPRINT",FACE,{"disambiguationData":[TD([[makeQuery(id+"F10.imprint","IMPRINT",EDGE,{"derivedFrom":sQuery(id+"F10.wireOp",EDGE,"E477")}),1.0]])]});
            extrude(context, id + "F12", {"entities" : qUnion([Q0]), "depth" : 6 * mm, "offsetDistance" : 25 * mm});
        }
        {
            var Q0;
            Q0=makeQuery(id+"F11.imprint","IMPRINT",FACE,{"disambiguationData":[TD([[makeQuery(id+"F11.imprint","IMPRINT",EDGE,{"derivedFrom":sQuery(id+"F11.wireOp",EDGE,"E479")}),-1.0]])]});
            extrude(context, id + "F13", {"entities" : qUnion([Q0]), "depth" : 11 * mm, "offsetDistance" : 25 * mm});
        }
        {
            var Q0;
            Q0=qCreatedBy(makeId("Front.planeOp"),FACE);
            var sketch = newSketch(context, id + "F14", { "sketchPlane" : qUnion([Q0])});
            skLineSegment(sketch, "E481", {"start": v(201.87, 52.26) * mm, "end": v(287.87, 52.26) * mm});
            skLineSegment(sketch, "E482", {"start": v(201.87, 127.26) * mm, "end": v(287.87, 127.26) * mm});
            skLineSegment(sketch, "E483", {"start": v(201.87, 127.26) * mm, "end": v(201.87, 52.26) * mm});
            skLineSegment(sketch, "E484", {"start": v(287.87, 127.26) * mm, "end": v(287.87, 52.26) * mm});
            skCircle(sketch, "E485", {"center": v(208.87, 59.26) * mm, "radius": 2.5 * mm});
            skCircle(sketch, "E486", {"center": v(280.87, 59.26) * mm, "radius": 2.5 * mm});
            skCircle(sketch, "E487", {"center": v(208.87, 120.26) * mm, "radius": 2.5 * mm});
            skCircle(sketch, "E488", {"center": v(280.87, 120.26) * mm, "radius": 2.5 * mm});
            skLineSegment(sketch, "E489", {"start": v(268.87, 124.81) * mm, "end": v(268.87, 54.71) * mm});
            skLineSegment(sketch, "E490", {"start": v(220.87, 124.81) * mm, "end": v(220.87, 54.71) * mm});
            skLineSegment(sketch, "E491", {"start": v(228.87, 124.81) * mm, "end": v(228.87, 54.71) * mm});
            skLineSegment(sketch, "E492", {"start": v(260.87, 124.81) * mm, "end": v(260.87, 54.71) * mm});
            skLineSegment(sketch, "E493", {"start": v(220.87, 124.81) * mm, "end": v(228.87, 124.81) * mm});
            skLineSegment(sketch, "E494", {"start": v(260.87, 124.81) * mm, "end": v(268.87, 124.81) * mm});
            skLineSegment(sketch, "E495", {"start": v(220.87, 54.71) * mm, "end": v(228.87, 54.71) * mm});
            skLineSegment(sketch, "E496", {"start": v(260.87, 54.71) * mm, "end": v(268.87, 54.71) * mm});
            skSolve(sketch);
        }
        {
            var Q0;
            Q0=qCreatedBy(makeId("Front.planeOp"),FACE);
            var sketch = newSketch(context, id + "F15", { "sketchPlane" : qUnion([Q0])});
            skCircle(sketch, "E497", {"center": v(-116.03, 197.93) * mm, "radius": 3 * mm});
            skLineSegment(sketch, "E498", {"start": v(-151.03, 147.93) * mm, "end": v(-81.03, 147.93) * mm});
            skLineSegment(sketch, "E499", {"start": v(-81.03, 147.93) * mm, "end": v(-81.03, 148.56) * mm});
            skLineSegment(sketch, "E500", {"start": v(-151.03, 147.93) * mm, "end": v(-151.03, 148.56) * mm});
            skLineSegment(sketch, "E501", {"start": v(-136.83, 162.33) * mm, "end": v(-125.63, 200.73) * mm});
            skLineSegment(sketch, "E502", {"start": v(-106.43, 200.73) * mm, "end": v(-95.23, 162.33) * mm});
            skArc(sketch, "E503", {"start": v(-95.23, 162.33) * mm, "mid": v(-89.95, 153.57) * mm, "end": v(-81.03, 148.56) * mm});
            skArc(sketch, "E504", {"start": v(-151.03, 148.56) * mm, "mid": v(-142.1, 153.57) * mm, "end": v(-136.83, 162.33) * mm});
            skArc(sketch, "E505", {"start": v(-106.43, 200.73) * mm, "mid": v(-116.03, 207.93) * mm, "end": v(-125.63, 200.73) * mm});
            skArc(sketch, "E506", {"start": v(-103.3, 190) * mm, "mid": v(-116.03, 212.93) * mm, "end": v(-128.76, 190) * mm});
            skSolve(sketch);
        }
        {
            var Q0;
            {var subQ0=sQuery(id+"F15.wireOp",EDGE,"E505");Q0=makeQuery(id+"F15.imprint","IMPRINT",FACE,{"disambiguationData":[TD([[makeQuery(id+"F15.imprint","IMPRINT",EDGE,{"derivedFrom":subQ0}),-1.0]])]});}
            extrude(context, id + "F16", {"entities" : qUnion([Q0]), "depth" : 4 * mm, "offsetDistance" : 25 * mm});
        }
        {
            var Q0;
            Q0=makeQuery(id+"F15.imprint","IMPRINT",FACE,{"disambiguationData":[TD([[makeQuery(id+"F15.imprint","IMPRINT",EDGE,{"derivedFrom":sQuery(id+"F15.wireOp",EDGE,"E497")}),1.0]])]});
            extrude(context, id + "F17", {"entities" : qUnion([Q0]), "operationType" : NewBodyOperationType.ADD, "depth" : 8 * mm, "offsetDistance" : 25 * mm});
        }
        {
            var Q0;
            Q0=makeQuery(id+"F14.imprint","IMPRINT",FACE,{"disambiguationData":[TD([[makeQuery(id+"F14.imprint","IMPRINT",EDGE,{"derivedFrom":sQuery(id+"F14.wireOp",EDGE,"E481")}),1.0]])]});
            extrude(context, id + "F18", {"entities" : qUnion([Q0]), "depth" : 5 * mm, "offsetDistance" : 25 * mm});
        }
        {
            var Q0;
            Q0=makeQuery(id+"F14.imprint","IMPRINT",FACE,{"disambiguationData":[TD([[makeQuery(id+"F14.imprint","IMPRINT",EDGE,{"derivedFrom":sQuery(id+"F14.wireOp",EDGE,"E490")}),1.0]])]});
            var Q1;
            Q1=makeQuery(id+"F14.imprint","IMPRINT",FACE,{"disambiguationData":[TD([[makeQuery(id+"F14.imprint","IMPRINT",EDGE,{"derivedFrom":sQuery(id+"F14.wireOp",EDGE,"E489")}),-1.0]])]});
            extrude(context, id + "F19", {"entities" : qUnion([Q0, Q1]), "operationType" : NewBodyOperationType.ADD, "depth" : 4.7 * mm, "offsetDistance" : 25 * mm});
        }
        {
            var Q0;
            Q0=qCreatedBy(makeId("Front.planeOp"),FACE);
            var sketch = newSketch(context, id + "F20", { "sketchPlane" : qUnion([Q0])});
            skCircle(sketch, "E507", {"center": v(238.58, 9.28) * mm, "radius": 2.5 * mm});
            skCircle(sketch, "E508", {"center": v(273.58, 9.28) * mm, "radius": 3 * mm});
            skLineSegment(sketch, "E509", {"start": v(250.58, -0.72) * mm, "end": v(250.58, 19.28) * mm});
            skLineSegment(sketch, "E510", {"start": v(250.58, 19.28) * mm, "end": v(253.58, 19.28) * mm});
            skLineSegment(sketch, "E511", {"start": v(250.58, -0.72) * mm, "end": v(253.58, -0.72) * mm});
            skLineSegment(sketch, "E512", {"start": v(253.58, 19.28) * mm, "end": v(260.58, 9.28) * mm});
            skLineSegment(sketch, "E513", {"start": v(260.58, 9.28) * mm, "end": v(253.58, -0.72) * mm});
            skArc(sketch, "E514", {"start": v(273.58, -0.72) * mm, "mid": v(280.65, 2.2) * mm, "end": v(283.58, 9.28) * mm});
            skArc(sketch, "E515", {"start": v(283.58, 9.28) * mm, "mid": v(280.65, 16.35) * mm, "end": v(273.58, 19.28) * mm});
            skLineSegment(sketch, "E516", {"start": v(238.58, 19.28) * mm, "end": v(273.58, 19.28) * mm});
            skArc(sketch, "E517", {"start": v(238.58, 19.28) * mm, "mid": v(231.5, 16.35) * mm, "end": v(228.58, 9.28) * mm});
            skLineSegment(sketch, "E518", {"start": v(238.58, -0.72) * mm, "end": v(273.58, -0.72) * mm});
            skArc(sketch, "E519", {"start": v(228.58, 9.28) * mm, "mid": v(231.5, 2.2) * mm, "end": v(238.58, -0.72) * mm});
            skCircle(sketch, "E520", {"center": v(273.58, 9.28) * mm, "radius": 7.5 * mm});
            skSolve(sketch);
        }
        {
            var Q0;
            Q0=makeQuery(id+"F20.imprint","IMPRINT",FACE,{"disambiguationData":[TD([[makeQuery(id+"F20.imprint","IMPRINT",EDGE,{"derivedFrom":sQuery(id+"F20.wireOp",EDGE,"E507")}),1.0]])]});
            var Q1;
            {var subQ3=sQuery(id+"F20.wireOp",EDGE,"E512");Q1=makeQuery(id+"F20.imprint","IMPRINT",FACE,{"disambiguationData":[TD([[makeQuery(id+"F20.imprint","IMPRINT",EDGE,{"derivedFrom":subQ3}),1.0]])]});}
            extrude(context, id + "F21", {"entities" : qUnion([Q0, Q1]), "depth" : 5 * mm, "offsetDistance" : 25 * mm});
        }
        {
            var Q0;
            Q0=makeQuery(id+"F20.imprint","IMPRINT",FACE,{"disambiguationData":[TD([[makeQuery(id+"F20.imprint","IMPRINT",EDGE,{"derivedFrom":sQuery(id+"F20.wireOp",EDGE,"E508")}),1.0]])]});
            extrude(context, id + "F22", {"entities" : qUnion([Q0]), "operationType" : NewBodyOperationType.ADD, "depth" : 5 * mm, "offsetDistance" : 25 * mm, "hasSecondDirection" : true, "secondDirectionOppositeDirection" : true, "secondDirectionDepth" : -0.2 * mm});
        }
        {
            var Q0;
            {var subQ2=sQuery(id+"F20.wireOp",EDGE,"E509");Q0=makeQuery(id+"F20.imprint","IMPRINT",FACE,{"disambiguationData":[TD([[makeQuery(id+"F20.imprint","IMPRINT",EDGE,{"derivedFrom":subQ2}),-1.0]])]});}
            extrude(context, id + "F23", {"entities" : qUnion([Q0]), "depth" : 13 * mm, "offsetDistance" : 25 * mm});
        }
    });
